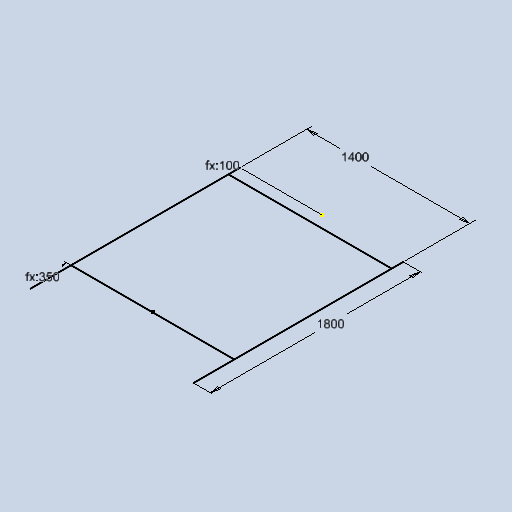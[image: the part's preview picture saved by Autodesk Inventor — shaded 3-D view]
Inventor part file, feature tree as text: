
AUTODESK INVENTOR PART (.ipt)
format: ipt  version: 2025 (Build 290162010, 162A)  size: 85,504 bytes
history: native  units: in
note: dims shown in document units (in); Inventor stores cm internally (conversion verified against a paired STEP export)
features: sketch x1
ambient origin geometry x8: Origin, YZ Plane, XZ Plane, XY Plane, X Axis, Y Axis, Z Axis, Center Point
feature tree (1):
  sketch  "Sketch3"  dims[d7=55.1181in d9=70.8661in d11=13.7795in d12=3.937in]
